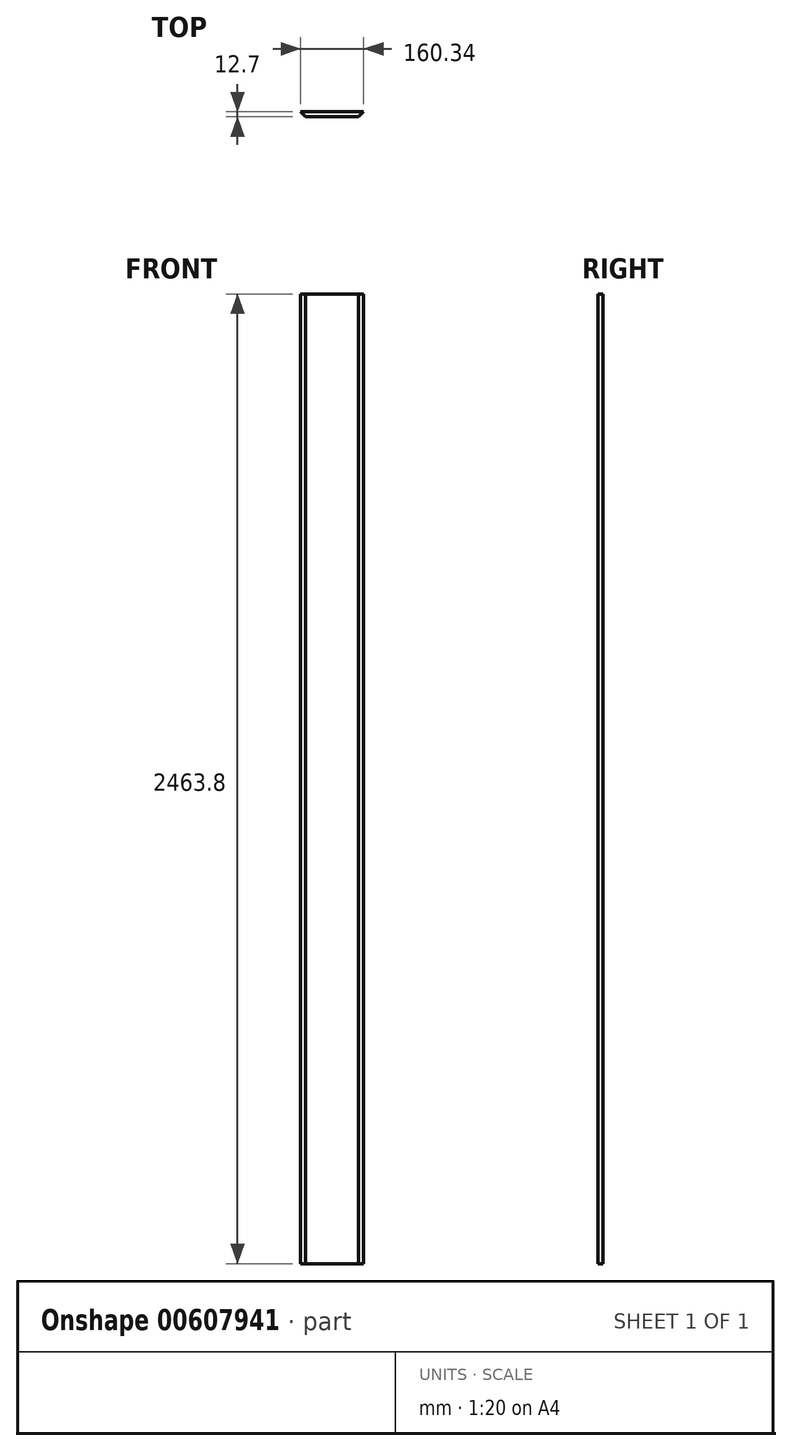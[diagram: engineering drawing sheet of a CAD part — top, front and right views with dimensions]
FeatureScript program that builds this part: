
annotation { "Feature Type Name" : "Feature", "Feature Type Description" : "" }
export const myFeature = defineFeature(function(context is Context, id is Id, definition is map)
    precondition{}
    {
        {
            var Q0;
            Q0=qCreatedBy(makeId("Top.planeOp"),FACE);
            var sketch = newSketch(context, id + "F0", { "sketchPlane" : qUnion([Q0])});
            skLineSegment(sketch, "E0.bottom", {"start": v(67.47, -6.35) * mm, "end": v(-67.47, -6.35) * mm});
            skLineSegment(sketch, "E0.top", {"start": v(67.47, 6.35) * mm, "end": v(-67.47, 6.35) * mm});
            skPoint(sketch, "E0.middle", {"position": v(0, 0) * mm});
            skLineSegment(sketch, "E1", {"start": v(-67.47, -6.35) * mm, "end": v(-80.17, 6.35) * mm});
            skLineSegment(sketch, "E2", {"start": v(-80.17, 6.35) * mm, "end": v(-67.47, 6.35) * mm});
            skLineSegment(sketch, "E3.MirrorCS", {"start": v(67.47, -6.35) * mm, "end": v(80.17, 6.35) * mm});
            skLineSegment(sketch, "E4.MirrorCS", {"start": v(80.17, 6.35) * mm, "end": v(67.47, 6.35) * mm});
            skSolve(sketch);
        }
        {
            var Q0;
            Q0=makeQuery(id+"F0.imprint","IMPRINT",FACE,{"disambiguationData":[TD([[makeQuery(id+"F0.imprint","IMPRINT",EDGE,{"derivedFrom":sQuery(id+"F0.wireOp",EDGE,"E0.bottom")}),-1.0]])]});
            extrude(context, id + "F1", {"entities" : qUnion([Q0]), "endBound" : BoundingType.SYMMETRIC, "depth" : 2463.8 * mm, "offsetDistance" : 25.4 * mm});
        }
    });
